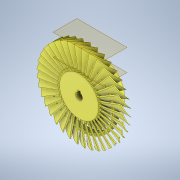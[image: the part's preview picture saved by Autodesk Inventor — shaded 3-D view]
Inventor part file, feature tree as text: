
AUTODESK INVENTOR PART (.ipt)
format: ipt  version: 2021.2 (Build 252289000, 289)  size: 4,642,304 bytes
history: native  units: in
note: dims shown in document units (in); Inventor stores cm internally (conversion verified against a paired STEP export)
features: sketch x6, extrude x4, plane x2, loft x1, pattern_circular x1, revolve x1, other x1
ambient origin geometry x8: Origin, YZ Plane, XZ Plane, XY Plane, X Axis, Y Axis, Z Axis, Center Point
bodies: Solid1 (feature_tree)
feature tree (16):
  extrude  "Extrusion1"  Depth=1.0in
  plane  "Work Plane1"
  extrude  "Extrusion2"  Depth=0.0312in
  plane  "Work Plane2"
  loft  "Loft1"
  pattern_circular  "Circular Pattern1"  Count=36 Angle=360.0deg
  revolve  "Revolution1"  [1 undecoded]
  extrude  "Extrusion3"  Depth=0.05in
  extrude  "Extrusion4"  Depth=0.5in
  sketch  "Sketch1"  dims[d0=1.8in d1=1.0in d2=0.0777in]
  sketch  "Sketch2"  dims[d3=1.0in d4=0.0312in]
  sketch  "Sketch3"  dims[d5=0.5in d6=0.0in d7=2.0in]
  other  "Edges1"
  sketch  "Sketch4"  dims[d8=0.0in d9=90.0deg]
  sketch  "Sketch5"  dims[d10=0.0in d11=90.0deg d12=14.1732in d13=360.0deg]
  sketch  "Sketch6"  dims[d15=0.125in d16=0.3in d17=0.05in d18=0.5in d20=0.6in d21=90.0deg d22=0.315in d23=0.125in d24=0.125in d25=0.0in d26=0.0in d27=3.9375in d28=0.0in d29=0.0in]
note: 1 required parameter value undecoded (feature->parameter linkage not recoverable at this tier; creation-order binding heuristic only, values carry confidence <= 0.55)
